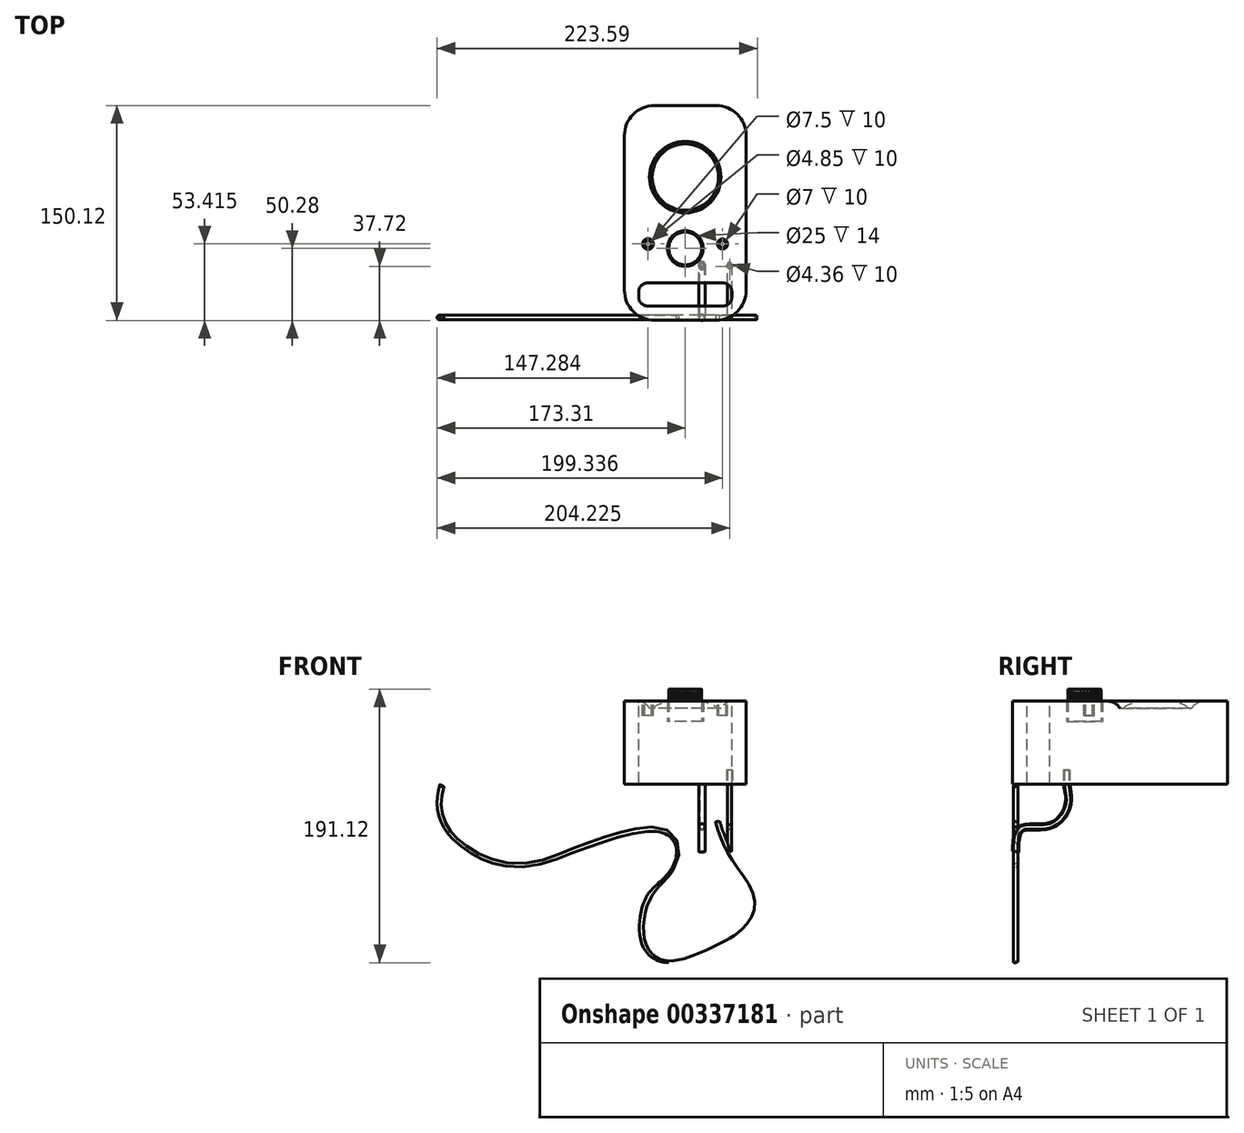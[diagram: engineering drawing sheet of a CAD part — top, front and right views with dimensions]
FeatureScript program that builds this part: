
annotation { "Feature Type Name" : "Feature", "Feature Type Description" : "" }
export const myFeature = defineFeature(function(context is Context, id is Id, definition is map)
    precondition{}
    {
        {
            var Q0;
            Q0=qCreatedBy(makeId("Top.planeOp"),FACE);
            var sketch = newSketch(context, id + "F0", { "sketchPlane" : qUnion([Q0])});
            skLineSegment(sketch, "E0.bottom", {"start": v(0, 150) * mm, "end": v(85, 150) * mm});
            skLineSegment(sketch, "E0.top", {"start": v(0, 0) * mm, "end": v(85, 0) * mm});
            skLineSegment(sketch, "E0.left", {"start": v(0, 150) * mm, "end": v(0, 0) * mm});
            skLineSegment(sketch, "E0.right", {"start": v(85, 150) * mm, "end": v(85, 0) * mm});
            skCircle(sketch, "E1", {"center": v(42.5, 100) * mm, "radius": 25 * mm});
            skLineSegment(sketch, "E2", {"start": v(42.5, 100) * mm, "end": v(-105.98, 100) * mm});
            skSolve(sketch);
        }
        {
            var Q0;
            Q0=makeQuery(id+"F0.imprint","IMPRINT",FACE,{"disambiguationData":[TD([[makeQuery(id+"F0.imprint","IMPRINT",EDGE,{"derivedFrom":sQuery(id+"F0.wireOp",EDGE,"E1")}),1.0]])]});
            extrude(context, id + "F1", {"entities" : qUnion([Q0]), "depth" : 53 * mm});
        }
        {
            var Q0;
            {var subQ1=sQuery(id+"F0.wireOp",EDGE,"E0.bottom");Q0=makeQuery(id+"F0.imprint","IMPRINT",FACE,{"disambiguationData":[TD([[makeQuery(id+"F0.imprint","IMPRINT",EDGE,{"derivedFrom":subQ1}),-1.0]])]});}
            extrude(context, id + "F2", {"entities" : qUnion([Q0]), "operationType" : NewBodyOperationType.ADD, "depth" : 58 * mm});
        }
        {
            var Q0;
            Q0=makeQuery(id+"F2.opExtrude","CAP_FACE",FACE,{"disambiguationData":[OSD([sQuery(id+"F0.wireOp",EDGE,"E0.bottom"),sQuery(id+"F0.wireOp",EDGE,"E0.top"),sQuery(id+"F0.wireOp",EDGE,"E0.left"),sQuery(id+"F0.wireOp",EDGE,"E0.right"),sQuery(id+"F0.wireOp",EDGE,"E1")])],"isStart":false});
            var sketch = newSketch(context, id + "F3", { "sketchPlane" : qUnion([Q0])});
            skLineSegment(sketch, "E3.bottom", {"start": v(42.5, 10) * mm, "end": v(16, 10) * mm});
            skLineSegment(sketch, "E3.top", {"start": v(42.5, 26) * mm, "end": v(16, 26) * mm});
            skLineSegment(sketch, "E3.right", {"start": v(10, 16) * mm, "end": v(10, 20) * mm});
            skPoint(sketch, "E4.visualSharp", {"position": v(10, 26) * mm});
            skArc(sketch, "E4.filletArc", {"start": v(16, 26) * mm, "mid": v(11.76, 24.24) * mm, "end": v(10, 20) * mm});
            skPoint(sketch, "E5.visualSharp", {"position": v(10, 10) * mm});
            skArc(sketch, "E5.filletArc", {"start": v(10, 16) * mm, "mid": v(11.76, 11.76) * mm, "end": v(16, 10) * mm});
            skArc(sketch, "E6.MirrorCS", {"start": v(69, 26) * mm, "mid": v(73.24, 24.24) * mm, "end": v(75, 20) * mm});
            skArc(sketch, "E7.MirrorCS", {"start": v(75, 16) * mm, "mid": v(73.24, 11.76) * mm, "end": v(69, 10) * mm});
            skLineSegment(sketch, "E8.MirrorCS", {"start": v(75, 16) * mm, "end": v(75, 20) * mm});
            skLineSegment(sketch, "E9.MirrorCS", {"start": v(42.5, 26) * mm, "end": v(69, 26) * mm});
            skLineSegment(sketch, "E10.MirrorCS", {"start": v(42.5, 10) * mm, "end": v(69, 10) * mm});
            skSolve(sketch);
        }
        {
            var Q0;
            Q0=makeQuery(id+"F2.opExtrude","CAP_EDGE",EDGE,{"disambiguationData":[OSD([sQuery(id+"F0.wireOp",EDGE,"E1")])],"isStart":false});
            fillet(context, id + "F4", {"entities" : qUnion([Q0]), "radius" : 10 * mm, "tangentPropagation" : true, "allowEdgeOverflow" : false});
        }
        {
            var Q0;
            Q0=makeQuery(id+"F2.opExtrude","SWEPT_EDGE",EDGE,{"disambiguationData":[OSD([sQuery(id+"F0.wireOp",EDGE,"E0.bottom"),sQuery(id+"F0.wireOp",EDGE,"E0.right")])]});
            var Q1;
            Q1=makeQuery(id+"F2.opExtrude","SWEPT_EDGE",EDGE,{"disambiguationData":[OSD([sQuery(id+"F0.wireOp",EDGE,"E0.top"),sQuery(id+"F0.wireOp",EDGE,"E0.right")])]});
            var Q2;
            Q2=makeQuery(id+"F2.opExtrude","SWEPT_EDGE",EDGE,{"disambiguationData":[OSD([sQuery(id+"F0.wireOp",EDGE,"E0.top"),sQuery(id+"F0.wireOp",EDGE,"E0.left")])]});
            var Q3;
            Q3=makeQuery(id+"F2.opExtrude","SWEPT_EDGE",EDGE,{"disambiguationData":[OSD([sQuery(id+"F0.wireOp",EDGE,"E0.bottom"),sQuery(id+"F0.wireOp",EDGE,"E0.left")])]});
            fillet(context, id + "F5", {"entities" : qUnion([Q0, Q1, Q2, Q3]), "radius" : 21 * mm, "tangentPropagation" : true, "allowEdgeOverflow" : false});
        }
        {
            var Q0;
            Q0=makeQuery(id+"F3.imprint","IMPRINT",FACE,{"disambiguationData":[TD([[makeQuery(id+"F3.imprint","IMPRINT",EDGE,{"derivedFrom":sQuery(id+"F3.wireOp",EDGE,"E3.bottom")}),-1.0]])]});
            extrude(context, id + "F6", {"entities" : qUnion([Q0]), "operationType" : NewBodyOperationType.REMOVE, "oppositeDirection" : true, "depth" : 60 * mm});
        }
        {
            var Q0;
            Q0=makeQuery(id+"F6.boolean.opBoolean","COPY",EDGE,{"derivedFrom":makeQuery(id+"F6.opExtrude","CAP_EDGE",EDGE,{"disambiguationData":[OSD([sQuery(id+"F3.wireOp",EDGE,"E3.top"),sQuery(id+"F3.wireOp",EDGE,"E9.MirrorCS")])],"isStart":true})});
            var Q1;
            Q1=makeQuery(id+"F6.boolean.opBoolean","COPY",EDGE,{"derivedFrom":makeQuery(id+"F6.opExtrude","CAP_EDGE",EDGE,{"disambiguationData":[OSD([sQuery(id+"F3.wireOp",EDGE,"E3.bottom"),sQuery(id+"F3.wireOp",EDGE,"E10.MirrorCS")])],"isStart":true})});
            var Q2;
            {var subQ0=sQuery(id+"F0.wireOp",EDGE,"E1");Q2=makeQuery(id+"F6.boolean.opBoolean","INTERSECT",EDGE,{"derivedFrom":[makeQuery(id+"F2.boolean.opBoolean","MERGE",FACE,{"derivedFrom":[makeQuery(id+"F1.opExtrude","CAP_FACE",FACE,{"disambiguationData":[OSD([subQ0])],"isStart":true}),makeQuery(id+"F2.opExtrude","CAP_FACE",FACE,{"disambiguationData":[OSD([sQuery(id+"F0.wireOp",EDGE,"E0.bottom"),sQuery(id+"F0.wireOp",EDGE,"E0.top"),sQuery(id+"F0.wireOp",EDGE,"E0.left"),sQuery(id+"F0.wireOp",EDGE,"E0.right"),subQ0])],"isStart":true})]}),makeQuery(id+"F6.opExtrude","SWEPT_FACE",FACE,{"disambiguationData":[OSD([sQuery(id+"F3.wireOp",EDGE,"E3.top"),sQuery(id+"F3.wireOp",EDGE,"E9.MirrorCS")])]})]});}
            fillet(context, id + "F7", {"entities" : qUnion([Q0, Q1, Q2]), "radius" : 1 * mm, "tangentPropagation" : true, "allowEdgeOverflow" : false});
        }
        {
            var Q0;
            Q0=makeQuery(id+"F2.opExtrude","CAP_FACE",FACE,{"disambiguationData":[OSD([sQuery(id+"F0.wireOp",EDGE,"E0.bottom"),sQuery(id+"F0.wireOp",EDGE,"E0.top"),sQuery(id+"F0.wireOp",EDGE,"E0.left"),sQuery(id+"F0.wireOp",EDGE,"E0.right"),sQuery(id+"F0.wireOp",EDGE,"E1")])],"isStart":false});
            var sketch = newSketch(context, id + "F8", { "sketchPlane" : qUnion([Q0])});
            skCircle(sketch, "E11", {"center": v(16.47, 53.3) * mm, "radius": 3.5 * mm});
            skLineSegment(sketch, "E12", {"start": v(42.5, 27) * mm, "end": v(42.5, 63.5) * mm});
            skCircle(sketch, "E13.0", {"center": v(16.47, 53.3) * mm, "radius": 3.75 * mm});
            skCircle(sketch, "E14", {"center": v(16.47, 53.3) * mm, "radius": 2.43 * mm});
            skCircle(sketch, "E15.MirrorC", {"center": v(68.53, 53.3) * mm, "radius": 3.5 * mm});
            skCircle(sketch, "E16.MirrorC", {"center": v(68.53, 53.3) * mm, "radius": 3.75 * mm});
            skCircle(sketch, "E17.MirrorC", {"center": v(68.53, 53.3) * mm, "radius": 2.43 * mm});
            skSolve(sketch);
        }
        {
            var Q0;
            Q0=makeQuery(id+"F8.imprint","IMPRINT",FACE,{"disambiguationData":[TD([[makeQuery(id+"F8.imprint","IMPRINT",EDGE,{"derivedFrom":sQuery(id+"F8.wireOp",EDGE,"E11")}),-1.0]])]});
            var Q1;
            Q1=makeQuery(id+"F8.imprint","IMPRINT",FACE,{"disambiguationData":[TD([[makeQuery(id+"F8.imprint","IMPRINT",EDGE,{"derivedFrom":sQuery(id+"F8.wireOp",EDGE,"E14")}),1.0]])]});
            var Q2;
            Q2=makeQuery(id+"F8.imprint","IMPRINT",FACE,{"disambiguationData":[TD([[makeQuery(id+"F8.imprint","IMPRINT",EDGE,{"derivedFrom":sQuery(id+"F8.wireOp",EDGE,"E15.MirrorC")}),1.0]])]});
            var Q3;
            Q3=makeQuery(id+"F8.imprint","IMPRINT",FACE,{"disambiguationData":[TD([[makeQuery(id+"F8.imprint","IMPRINT",EDGE,{"derivedFrom":sQuery(id+"F8.wireOp",EDGE,"E17.MirrorC")}),-1.0]])]});
            extrude(context, id + "F9", {"entities" : qUnion([Q0, Q1, Q2, Q3]), "operationType" : NewBodyOperationType.REMOVE, "oppositeDirection" : true, "depth" : 10 * mm});
        }
        {
            var Q0;
            {var subQ1=sQuery(id+"F0.wireOp",EDGE,"E0.bottom");Q0=makeQuery(id+"F0.imprint","IMPRINT",FACE,{"disambiguationData":[TD([[makeQuery(id+"F0.imprint","IMPRINT",EDGE,{"derivedFrom":subQ1}),-1.0]])]});}
            var sketch = newSketch(context, id + "F10", { "sketchPlane" : qUnion([Q0])});
            skCircle(sketch, "E18", {"center": v(42.5, 50.16) * mm, "radius": 12.5 * mm});
            skSolve(sketch);
        }
        {
            var Q0;
            Q0 = qSketchRegion(id + "F10", true);
            extrude(context, id + "F11", {"entities" : qUnion([Q0]), "operationType" : NewBodyOperationType.REMOVE, "depth" : 100 * mm, "hasSecondDirection" : true, "secondDirectionOppositeDirection" : true, "secondDirectionDepth" : -44 * mm});
        }
        {
            var Q0;
            Q0=makeQuery(id+"F11.boolean.opBoolean","COPY",FACE,{"derivedFrom":makeQuery(id+"F11.opExtrude","CAP_FACE",FACE,{"disambiguationData":[OSD([sQuery(id+"F10.wireOp",EDGE,"E18")])],"isStart":true})});
            var sketch = newSketch(context, id + "F12", { "sketchPlane" : qUnion([Q0])});
            skCircle(sketch, "E19", {"center": v(42.5, 50.16) * mm, "radius": 11.52 * mm});
            skSolve(sketch);
        }
        {
            var Q0;
            Q0=makeQuery(id+"F12.imprint","IMPRINT",FACE,{"disambiguationData":[TD([[makeQuery(id+"F12.imprint","IMPRINT",EDGE,{"derivedFrom":sQuery(id+"F12.wireOp",EDGE,"E19")}),1.0]])]});
            extrude(context, id + "F13", {"entities" : qUnion([Q0]), "depth" : 22.5 * mm});
        }
        {
            var Q0;
            Q0=makeQuery(id+"F13.opExtrude","CAP_EDGE",EDGE,{"disambiguationData":[OSD([sQuery(id+"F12.wireOp",EDGE,"E19")])],"isStart":false});
            fillet(context, id + "F14", {"entities" : qUnion([Q0]), "radius" : 0.5 * mm, "tangentPropagation" : true, "allowEdgeOverflow" : false});
        }
        {
            var Q0;
            Q0=makeQuery(id+"F13.opExtrude","CAP_FACE",FACE,{"disambiguationData":[OSD([sQuery(id+"F12.wireOp",EDGE,"E19")])],"isStart":false});
            var sketch = newSketch(context, id + "F15", { "sketchPlane" : qUnion([Q0])});
            skLineSegment(sketch, "E20", {"start": v(42.5, 61.18) * mm, "end": v(42.13, 61.81) * mm});
            skLineSegment(sketch, "E21.MirrorCS", {"start": v(42.5, 61.18) * mm, "end": v(42.87, 61.81) * mm});
            skLineSegment(sketch, "E22", {"start": v(42.13, 61.81) * mm, "end": v(42.87, 61.81) * mm});
            skPoint(sketch, "E23.start.orphan", {"position": v(42.5, 50.16) * mm});
            skLineSegment(sketch, "E24.1.0", {"start": v(41.44, 61.13) * mm, "end": v(41.75, 61.8) * mm});
            skLineSegment(sketch, "E24.1.1", {"start": v(41, 61.72) * mm, "end": v(41.75, 61.8) * mm});
            skLineSegment(sketch, "E24.1.2", {"start": v(41.44, 61.13) * mm, "end": v(41, 61.72) * mm});
            skLineSegment(sketch, "E24.2.0", {"start": v(40.38, 60.98) * mm, "end": v(40.63, 61.66) * mm});
            skLineSegment(sketch, "E24.2.1", {"start": v(39.9, 61.52) * mm, "end": v(40.63, 61.66) * mm});
            skLineSegment(sketch, "E24.2.2", {"start": v(40.38, 60.98) * mm, "end": v(39.9, 61.52) * mm});
            skLineSegment(sketch, "E25.1.3.0", {"start": v(39.35, 60.72) * mm, "end": v(39.53, 61.43) * mm});
            skLineSegment(sketch, "E25.3.3.0", {"start": v(38.81, 61.22) * mm, "end": v(39.53, 61.43) * mm});
            skLineSegment(sketch, "E25.6.3.0", {"start": v(39.35, 60.72) * mm, "end": v(38.81, 61.22) * mm});
            skLineSegment(sketch, "E25.1.4.0", {"start": v(38.34, 60.37) * mm, "end": v(38.45, 61.1) * mm});
            skLineSegment(sketch, "E25.3.4.0", {"start": v(37.76, 60.8) * mm, "end": v(38.45, 61.1) * mm});
            skLineSegment(sketch, "E25.6.4.0", {"start": v(38.34, 60.37) * mm, "end": v(37.76, 60.8) * mm});
            skLineSegment(sketch, "E25.1.5.0", {"start": v(37.38, 59.92) * mm, "end": v(37.42, 60.65) * mm});
            skLineSegment(sketch, "E25.3.5.0", {"start": v(36.75, 60.3) * mm, "end": v(37.42, 60.65) * mm});
            skLineSegment(sketch, "E25.6.5.0", {"start": v(37.38, 59.92) * mm, "end": v(36.75, 60.3) * mm});
            skLineSegment(sketch, "E25.1.6.0", {"start": v(36.46, 59.38) * mm, "end": v(36.43, 60.1) * mm});
            skLineSegment(sketch, "E25.3.6.0", {"start": v(35.8, 59.7) * mm, "end": v(36.43, 60.1) * mm});
            skLineSegment(sketch, "E25.6.6.0", {"start": v(36.46, 59.38) * mm, "end": v(35.8, 59.7) * mm});
            skLineSegment(sketch, "E25.1.7.0", {"start": v(35.6, 58.75) * mm, "end": v(35.5, 59.48) * mm});
            skLineSegment(sketch, "E25.3.7.0", {"start": v(34.91, 59) * mm, "end": v(35.5, 59.48) * mm});
            skLineSegment(sketch, "E25.6.7.0", {"start": v(35.6, 58.75) * mm, "end": v(34.91, 59) * mm});
            skLineSegment(sketch, "E25.1.8.0", {"start": v(34.8, 58.05) * mm, "end": v(34.63, 58.76) * mm});
            skLineSegment(sketch, "E25.3.8.0", {"start": v(34.1, 58.24) * mm, "end": v(34.63, 58.76) * mm});
            skLineSegment(sketch, "E25.6.8.0", {"start": v(34.8, 58.05) * mm, "end": v(34.1, 58.24) * mm});
            skLineSegment(sketch, "E25.1.9.0", {"start": v(34.08, 57.27) * mm, "end": v(33.84, 57.96) * mm});
            skLineSegment(sketch, "E25.3.9.0", {"start": v(33.35, 57.39) * mm, "end": v(33.84, 57.96) * mm});
            skLineSegment(sketch, "E25.6.9.0", {"start": v(34.08, 57.27) * mm, "end": v(33.35, 57.39) * mm});
            skLineSegment(sketch, "E25.1.10.0", {"start": v(33.43, 56.42) * mm, "end": v(33.12, 57.09) * mm});
            skLineSegment(sketch, "E25.3.10.0", {"start": v(32.7, 56.47) * mm, "end": v(33.12, 57.09) * mm});
            skLineSegment(sketch, "E25.6.10.0", {"start": v(33.43, 56.42) * mm, "end": v(32.7, 56.47) * mm});
            skLineSegment(sketch, "E25.1.11.0", {"start": v(32.87, 55.52) * mm, "end": v(32.5, 56.15) * mm});
            skLineSegment(sketch, "E25.3.11.0", {"start": v(32.14, 55.5) * mm, "end": v(32.5, 56.15) * mm});
            skLineSegment(sketch, "E25.6.11.0", {"start": v(32.87, 55.52) * mm, "end": v(32.14, 55.5) * mm});
            skLineSegment(sketch, "E25.1.12.0", {"start": v(32.4, 54.56) * mm, "end": v(31.97, 55.16) * mm});
            skLineSegment(sketch, "E25.3.12.0", {"start": v(31.67, 54.47) * mm, "end": v(31.97, 55.16) * mm});
            skLineSegment(sketch, "E25.6.12.0", {"start": v(32.4, 54.56) * mm, "end": v(31.67, 54.47) * mm});
            skLineSegment(sketch, "E25.1.13.0", {"start": v(32.02, 53.57) * mm, "end": v(31.54, 54.12) * mm});
            skLineSegment(sketch, "E25.3.13.0", {"start": v(31.3, 53.4) * mm, "end": v(31.54, 54.12) * mm});
            skLineSegment(sketch, "E25.6.13.0", {"start": v(32.02, 53.57) * mm, "end": v(31.3, 53.4) * mm});
            skLineSegment(sketch, "E25.1.14.0", {"start": v(31.74, 52.54) * mm, "end": v(31.2, 53.04) * mm});
            skLineSegment(sketch, "E25.3.14.0", {"start": v(31.04, 52.3) * mm, "end": v(31.2, 53.04) * mm});
            skLineSegment(sketch, "E25.6.14.0", {"start": v(31.74, 52.54) * mm, "end": v(31.04, 52.3) * mm});
            skLineSegment(sketch, "E25.1.15.0", {"start": v(31.56, 51.49) * mm, "end": v(30.98, 51.94) * mm});
            skLineSegment(sketch, "E25.3.15.0", {"start": v(30.89, 51.2) * mm, "end": v(30.98, 51.94) * mm});
            skLineSegment(sketch, "E25.6.15.0", {"start": v(31.56, 51.49) * mm, "end": v(30.89, 51.2) * mm});
            skLineSegment(sketch, "E25.1.16.0", {"start": v(31.48, 50.43) * mm, "end": v(30.86, 50.81) * mm});
            skLineSegment(sketch, "E25.3.16.0", {"start": v(30.84, 50.07) * mm, "end": v(30.86, 50.81) * mm});
            skLineSegment(sketch, "E25.6.16.0", {"start": v(31.48, 50.43) * mm, "end": v(30.84, 50.07) * mm});
            skLineSegment(sketch, "E25.1.17.0", {"start": v(31.5, 49.36) * mm, "end": v(30.85, 49.69) * mm});
            skLineSegment(sketch, "E25.3.17.0", {"start": v(30.9, 48.94) * mm, "end": v(30.85, 49.69) * mm});
            skLineSegment(sketch, "E25.6.17.0", {"start": v(31.5, 49.36) * mm, "end": v(30.9, 48.94) * mm});
            skLineSegment(sketch, "E25.1.18.0", {"start": v(31.64, 48.3) * mm, "end": v(30.95, 48.57) * mm});
            skLineSegment(sketch, "E25.3.18.0", {"start": v(31.08, 47.83) * mm, "end": v(30.95, 48.57) * mm});
            skLineSegment(sketch, "E25.6.18.0", {"start": v(31.64, 48.3) * mm, "end": v(31.08, 47.83) * mm});
            skLineSegment(sketch, "E25.1.19.0", {"start": v(31.87, 47.26) * mm, "end": v(31.16, 47.46) * mm});
            skLineSegment(sketch, "E25.3.19.0", {"start": v(31.36, 46.74) * mm, "end": v(31.16, 47.46) * mm});
            skLineSegment(sketch, "E25.6.19.0", {"start": v(31.87, 47.26) * mm, "end": v(31.36, 46.74) * mm});
            skLineSegment(sketch, "E25.1.20.0", {"start": v(32.2, 46.25) * mm, "end": v(31.47, 46.38) * mm});
            skLineSegment(sketch, "E25.3.20.0", {"start": v(31.74, 45.68) * mm, "end": v(31.47, 46.38) * mm});
            skLineSegment(sketch, "E25.6.20.0", {"start": v(32.2, 46.25) * mm, "end": v(31.74, 45.68) * mm});
            skLineSegment(sketch, "E25.1.21.0", {"start": v(32.62, 45.28) * mm, "end": v(31.9, 45.33) * mm});
            skLineSegment(sketch, "E25.3.21.0", {"start": v(32.22, 44.66) * mm, "end": v(31.9, 45.33) * mm});
            skLineSegment(sketch, "E25.6.21.0", {"start": v(32.62, 45.28) * mm, "end": v(32.22, 44.66) * mm});
            skLineSegment(sketch, "E25.1.22.0", {"start": v(33.14, 44.34) * mm, "end": v(32.4, 44.33) * mm});
            skLineSegment(sketch, "E25.3.22.0", {"start": v(32.8, 43.7) * mm, "end": v(32.4, 44.33) * mm});
            skLineSegment(sketch, "E25.6.22.0", {"start": v(33.14, 44.34) * mm, "end": v(32.8, 43.7) * mm});
            skLineSegment(sketch, "E25.1.23.0", {"start": v(33.74, 43.47) * mm, "end": v(33.02, 43.38) * mm});
            skLineSegment(sketch, "E25.3.23.0", {"start": v(33.47, 42.79) * mm, "end": v(33.02, 43.38) * mm});
            skLineSegment(sketch, "E25.6.23.0", {"start": v(33.74, 43.47) * mm, "end": v(33.47, 42.79) * mm});
            skLineSegment(sketch, "E25.1.24.0", {"start": v(34.43, 42.65) * mm, "end": v(33.71, 42.5) * mm});
            skLineSegment(sketch, "E25.3.24.0", {"start": v(34.22, 41.95) * mm, "end": v(33.71, 42.5) * mm});
            skLineSegment(sketch, "E25.6.24.0", {"start": v(34.43, 42.65) * mm, "end": v(34.22, 41.95) * mm});
            skLineSegment(sketch, "E25.1.25.0", {"start": v(35.2, 41.91) * mm, "end": v(34.5, 41.69) * mm});
            skLineSegment(sketch, "E25.3.25.0", {"start": v(35.05, 41.2) * mm, "end": v(34.5, 41.69) * mm});
            skLineSegment(sketch, "E25.6.25.0", {"start": v(35.2, 41.91) * mm, "end": v(35.05, 41.2) * mm});
            skLineSegment(sketch, "E25.1.26.0", {"start": v(36.02, 41.24) * mm, "end": v(35.35, 40.95) * mm});
            skLineSegment(sketch, "E25.3.26.0", {"start": v(35.95, 40.51) * mm, "end": v(35.35, 40.95) * mm});
            skLineSegment(sketch, "E25.6.26.0", {"start": v(36.02, 41.24) * mm, "end": v(35.95, 40.51) * mm});
            skLineSegment(sketch, "E25.1.27.0", {"start": v(36.91, 40.66) * mm, "end": v(36.27, 40.3) * mm});
            skLineSegment(sketch, "E25.3.27.0", {"start": v(36.92, 39.93) * mm, "end": v(36.27, 40.3) * mm});
            skLineSegment(sketch, "E25.6.27.0", {"start": v(36.91, 40.66) * mm, "end": v(36.92, 39.93) * mm});
            skLineSegment(sketch, "E25.1.28.0", {"start": v(37.86, 40.16) * mm, "end": v(37.25, 39.75) * mm});
            skLineSegment(sketch, "E25.3.28.0", {"start": v(37.93, 39.44) * mm, "end": v(37.25, 39.75) * mm});
            skLineSegment(sketch, "E25.6.28.0", {"start": v(37.86, 40.16) * mm, "end": v(37.93, 39.44) * mm});
            skLineSegment(sketch, "E25.1.29.0", {"start": v(38.84, 39.76) * mm, "end": v(38.28, 39.3) * mm});
            skLineSegment(sketch, "E25.3.29.0", {"start": v(38.99, 39.05) * mm, "end": v(38.28, 39.3) * mm});
            skLineSegment(sketch, "E25.6.29.0", {"start": v(38.84, 39.76) * mm, "end": v(38.99, 39.05) * mm});
            skLineSegment(sketch, "E25.1.30.0", {"start": v(39.86, 39.46) * mm, "end": v(39.35, 38.94) * mm});
            skLineSegment(sketch, "E25.3.30.0", {"start": v(40.07, 38.76) * mm, "end": v(39.35, 38.94) * mm});
            skLineSegment(sketch, "E25.6.30.0", {"start": v(39.86, 39.46) * mm, "end": v(40.07, 38.76) * mm});
            skLineSegment(sketch, "E25.1.31.0", {"start": v(40.9, 39.25) * mm, "end": v(40.45, 38.69) * mm});
            skLineSegment(sketch, "E25.3.31.0", {"start": v(41.19, 38.58) * mm, "end": v(40.45, 38.69) * mm});
            skLineSegment(sketch, "E25.6.31.0", {"start": v(40.9, 39.25) * mm, "end": v(41.19, 38.58) * mm});
            skLineSegment(sketch, "E25.1.32.0", {"start": v(41.97, 39.15) * mm, "end": v(41.56, 38.54) * mm});
            skLineSegment(sketch, "E25.3.32.0", {"start": v(42.31, 38.5) * mm, "end": v(41.56, 38.54) * mm});
            skLineSegment(sketch, "E25.6.32.0", {"start": v(41.97, 39.15) * mm, "end": v(42.31, 38.5) * mm});
            skLineSegment(sketch, "E25.1.33.0", {"start": v(43.03, 39.15) * mm, "end": v(42.69, 38.5) * mm});
            skLineSegment(sketch, "E25.3.33.0", {"start": v(43.44, 38.54) * mm, "end": v(42.69, 38.5) * mm});
            skLineSegment(sketch, "E25.6.33.0", {"start": v(43.03, 39.15) * mm, "end": v(43.44, 38.54) * mm});
            skLineSegment(sketch, "E25.1.34.0", {"start": v(44.1, 39.25) * mm, "end": v(43.81, 38.58) * mm});
            skLineSegment(sketch, "E25.3.34.0", {"start": v(44.55, 38.69) * mm, "end": v(43.81, 38.58) * mm});
            skLineSegment(sketch, "E25.6.34.0", {"start": v(44.1, 39.25) * mm, "end": v(44.55, 38.69) * mm});
            skLineSegment(sketch, "E25.1.35.0", {"start": v(45.14, 39.46) * mm, "end": v(44.93, 38.76) * mm});
            skLineSegment(sketch, "E25.3.35.0", {"start": v(45.65, 38.94) * mm, "end": v(44.93, 38.76) * mm});
            skLineSegment(sketch, "E25.6.35.0", {"start": v(45.14, 39.46) * mm, "end": v(45.65, 38.94) * mm});
            skLineSegment(sketch, "E25.1.36.0", {"start": v(46.16, 39.76) * mm, "end": v(46.01, 39.05) * mm});
            skLineSegment(sketch, "E25.3.36.0", {"start": v(46.72, 39.3) * mm, "end": v(46.01, 39.05) * mm});
            skLineSegment(sketch, "E25.6.36.0", {"start": v(46.16, 39.76) * mm, "end": v(46.72, 39.3) * mm});
            skLineSegment(sketch, "E25.1.37.0", {"start": v(47.14, 40.16) * mm, "end": v(47.07, 39.44) * mm});
            skLineSegment(sketch, "E25.3.37.0", {"start": v(47.75, 39.75) * mm, "end": v(47.07, 39.44) * mm});
            skLineSegment(sketch, "E25.6.37.0", {"start": v(47.14, 40.16) * mm, "end": v(47.75, 39.75) * mm});
            skLineSegment(sketch, "E25.1.38.0", {"start": v(48.09, 40.66) * mm, "end": v(48.08, 39.93) * mm});
            skLineSegment(sketch, "E25.3.38.0", {"start": v(48.73, 40.3) * mm, "end": v(48.08, 39.93) * mm});
            skLineSegment(sketch, "E25.6.38.0", {"start": v(48.09, 40.66) * mm, "end": v(48.73, 40.3) * mm});
            skLineSegment(sketch, "E25.1.39.0", {"start": v(48.98, 41.24) * mm, "end": v(49.05, 40.51) * mm});
            skLineSegment(sketch, "E25.3.39.0", {"start": v(49.65, 40.95) * mm, "end": v(49.05, 40.51) * mm});
            skLineSegment(sketch, "E25.6.39.0", {"start": v(48.98, 41.24) * mm, "end": v(49.65, 40.95) * mm});
            skLineSegment(sketch, "E25.1.40.0", {"start": v(49.8, 41.91) * mm, "end": v(49.95, 41.2) * mm});
            skLineSegment(sketch, "E25.3.40.0", {"start": v(50.5, 41.69) * mm, "end": v(49.95, 41.2) * mm});
            skLineSegment(sketch, "E25.6.40.0", {"start": v(49.8, 41.91) * mm, "end": v(50.5, 41.69) * mm});
            skLineSegment(sketch, "E25.1.41.0", {"start": v(50.57, 42.65) * mm, "end": v(50.78, 41.95) * mm});
            skLineSegment(sketch, "E25.3.41.0", {"start": v(51.29, 42.5) * mm, "end": v(50.78, 41.95) * mm});
            skLineSegment(sketch, "E25.6.41.0", {"start": v(50.57, 42.65) * mm, "end": v(51.29, 42.5) * mm});
            skLineSegment(sketch, "E25.1.42.0", {"start": v(51.26, 43.47) * mm, "end": v(51.53, 42.79) * mm});
            skLineSegment(sketch, "E25.3.42.0", {"start": v(51.98, 43.38) * mm, "end": v(51.53, 42.79) * mm});
            skLineSegment(sketch, "E25.6.42.0", {"start": v(51.26, 43.47) * mm, "end": v(51.98, 43.38) * mm});
            skLineSegment(sketch, "E25.1.43.0", {"start": v(51.86, 44.34) * mm, "end": v(52.2, 43.7) * mm});
            skLineSegment(sketch, "E25.3.43.0", {"start": v(52.6, 44.33) * mm, "end": v(52.2, 43.7) * mm});
            skLineSegment(sketch, "E25.6.43.0", {"start": v(51.86, 44.34) * mm, "end": v(52.6, 44.33) * mm});
            skLineSegment(sketch, "E25.1.44.0", {"start": v(52.38, 45.28) * mm, "end": v(52.78, 44.66) * mm});
            skLineSegment(sketch, "E25.3.44.0", {"start": v(53.1, 45.33) * mm, "end": v(52.78, 44.66) * mm});
            skLineSegment(sketch, "E25.6.44.0", {"start": v(52.38, 45.28) * mm, "end": v(53.1, 45.33) * mm});
            skLineSegment(sketch, "E25.1.45.0", {"start": v(52.8, 46.25) * mm, "end": v(53.26, 45.68) * mm});
            skLineSegment(sketch, "E25.3.45.0", {"start": v(53.53, 46.38) * mm, "end": v(53.26, 45.68) * mm});
            skLineSegment(sketch, "E25.6.45.0", {"start": v(52.8, 46.25) * mm, "end": v(53.53, 46.38) * mm});
            skLineSegment(sketch, "E25.1.46.0", {"start": v(53.13, 47.26) * mm, "end": v(53.64, 46.74) * mm});
            skLineSegment(sketch, "E25.3.46.0", {"start": v(53.84, 47.46) * mm, "end": v(53.64, 46.74) * mm});
            skLineSegment(sketch, "E25.6.46.0", {"start": v(53.13, 47.26) * mm, "end": v(53.84, 47.46) * mm});
            skLineSegment(sketch, "E25.1.47.0", {"start": v(53.36, 48.3) * mm, "end": v(53.92, 47.83) * mm});
            skLineSegment(sketch, "E25.3.47.0", {"start": v(54.05, 48.57) * mm, "end": v(53.92, 47.83) * mm});
            skLineSegment(sketch, "E25.6.47.0", {"start": v(53.36, 48.3) * mm, "end": v(54.05, 48.57) * mm});
            skLineSegment(sketch, "E25.1.48.0", {"start": v(53.5, 49.36) * mm, "end": v(54.1, 48.94) * mm});
            skLineSegment(sketch, "E25.3.48.0", {"start": v(54.15, 49.69) * mm, "end": v(54.1, 48.94) * mm});
            skLineSegment(sketch, "E25.6.48.0", {"start": v(53.5, 49.36) * mm, "end": v(54.15, 49.69) * mm});
            skLineSegment(sketch, "E25.1.49.0", {"start": v(53.52, 50.43) * mm, "end": v(54.16, 50.07) * mm});
            skLineSegment(sketch, "E25.3.49.0", {"start": v(54.14, 50.81) * mm, "end": v(54.16, 50.07) * mm});
            skLineSegment(sketch, "E25.6.49.0", {"start": v(53.52, 50.43) * mm, "end": v(54.14, 50.81) * mm});
            skLineSegment(sketch, "E26.1.50.0", {"start": v(53.44, 51.49) * mm, "end": v(54.11, 51.2) * mm});
            skLineSegment(sketch, "E26.3.50.0", {"start": v(54.02, 51.94) * mm, "end": v(54.11, 51.2) * mm});
            skLineSegment(sketch, "E26.6.50.0", {"start": v(53.44, 51.49) * mm, "end": v(54.02, 51.94) * mm});
            skLineSegment(sketch, "E26.1.51.0", {"start": v(53.26, 52.54) * mm, "end": v(53.96, 52.3) * mm});
            skLineSegment(sketch, "E26.3.51.0", {"start": v(53.8, 53.04) * mm, "end": v(53.96, 52.3) * mm});
            skLineSegment(sketch, "E26.6.51.0", {"start": v(53.26, 52.54) * mm, "end": v(53.8, 53.04) * mm});
            skLineSegment(sketch, "E26.1.52.0", {"start": v(52.98, 53.57) * mm, "end": v(53.7, 53.4) * mm});
            skLineSegment(sketch, "E26.3.52.0", {"start": v(53.46, 54.12) * mm, "end": v(53.7, 53.4) * mm});
            skLineSegment(sketch, "E26.6.52.0", {"start": v(52.98, 53.57) * mm, "end": v(53.46, 54.12) * mm});
            skLineSegment(sketch, "E26.1.53.0", {"start": v(52.6, 54.56) * mm, "end": v(53.33, 54.47) * mm});
            skLineSegment(sketch, "E26.3.53.0", {"start": v(53.03, 55.16) * mm, "end": v(53.33, 54.47) * mm});
            skLineSegment(sketch, "E26.6.53.0", {"start": v(52.6, 54.56) * mm, "end": v(53.03, 55.16) * mm});
            skLineSegment(sketch, "E26.1.54.0", {"start": v(52.13, 55.52) * mm, "end": v(52.86, 55.5) * mm});
            skLineSegment(sketch, "E26.3.54.0", {"start": v(52.5, 56.15) * mm, "end": v(52.86, 55.5) * mm});
            skLineSegment(sketch, "E26.6.54.0", {"start": v(52.13, 55.52) * mm, "end": v(52.5, 56.15) * mm});
            skLineSegment(sketch, "E26.1.55.0", {"start": v(51.57, 56.42) * mm, "end": v(52.3, 56.47) * mm});
            skLineSegment(sketch, "E26.3.55.0", {"start": v(51.88, 57.09) * mm, "end": v(52.3, 56.47) * mm});
            skLineSegment(sketch, "E26.6.55.0", {"start": v(51.57, 56.42) * mm, "end": v(51.88, 57.09) * mm});
            skLineSegment(sketch, "E26.1.56.0", {"start": v(50.92, 57.27) * mm, "end": v(51.65, 57.39) * mm});
            skLineSegment(sketch, "E26.3.56.0", {"start": v(51.16, 57.96) * mm, "end": v(51.65, 57.39) * mm});
            skLineSegment(sketch, "E26.6.56.0", {"start": v(50.92, 57.27) * mm, "end": v(51.16, 57.96) * mm});
            skLineSegment(sketch, "E26.1.57.0", {"start": v(50.2, 58.05) * mm, "end": v(50.9, 58.24) * mm});
            skLineSegment(sketch, "E26.3.57.0", {"start": v(50.37, 58.76) * mm, "end": v(50.9, 58.24) * mm});
            skLineSegment(sketch, "E26.6.57.0", {"start": v(50.2, 58.05) * mm, "end": v(50.37, 58.76) * mm});
            skLineSegment(sketch, "E26.1.58.0", {"start": v(49.4, 58.75) * mm, "end": v(50.09, 59) * mm});
            skLineSegment(sketch, "E26.3.58.0", {"start": v(49.5, 59.48) * mm, "end": v(50.09, 59) * mm});
            skLineSegment(sketch, "E26.6.58.0", {"start": v(49.4, 58.75) * mm, "end": v(49.5, 59.48) * mm});
            skLineSegment(sketch, "E26.1.59.0", {"start": v(48.54, 59.38) * mm, "end": v(49.2, 59.7) * mm});
            skLineSegment(sketch, "E26.3.59.0", {"start": v(48.57, 60.1) * mm, "end": v(49.2, 59.7) * mm});
            skLineSegment(sketch, "E26.6.59.0", {"start": v(48.54, 59.38) * mm, "end": v(48.57, 60.1) * mm});
            skLineSegment(sketch, "E27.1.60.0", {"start": v(47.62, 59.92) * mm, "end": v(48.25, 60.3) * mm});
            skLineSegment(sketch, "E27.3.60.0", {"start": v(47.58, 60.65) * mm, "end": v(48.25, 60.3) * mm});
            skLineSegment(sketch, "E27.6.60.0", {"start": v(47.62, 59.92) * mm, "end": v(47.58, 60.65) * mm});
            skLineSegment(sketch, "E27.1.61.0", {"start": v(46.66, 60.37) * mm, "end": v(47.24, 60.8) * mm});
            skLineSegment(sketch, "E27.3.61.0", {"start": v(46.55, 61.1) * mm, "end": v(47.24, 60.8) * mm});
            skLineSegment(sketch, "E27.6.61.0", {"start": v(46.66, 60.37) * mm, "end": v(46.55, 61.1) * mm});
            skLineSegment(sketch, "E27.1.62.0", {"start": v(45.65, 60.72) * mm, "end": v(46.19, 61.22) * mm});
            skLineSegment(sketch, "E27.3.62.0", {"start": v(45.47, 61.43) * mm, "end": v(46.19, 61.22) * mm});
            skLineSegment(sketch, "E27.6.62.0", {"start": v(45.65, 60.72) * mm, "end": v(45.47, 61.43) * mm});
            skLineSegment(sketch, "E27.1.63.0", {"start": v(44.62, 60.98) * mm, "end": v(45.1, 61.52) * mm});
            skLineSegment(sketch, "E27.3.63.0", {"start": v(44.37, 61.66) * mm, "end": v(45.1, 61.52) * mm});
            skLineSegment(sketch, "E27.6.63.0", {"start": v(44.62, 60.98) * mm, "end": v(44.37, 61.66) * mm});
            skLineSegment(sketch, "E27.1.64.0", {"start": v(43.56, 61.13) * mm, "end": v(44, 61.72) * mm});
            skLineSegment(sketch, "E27.3.64.0", {"start": v(43.25, 61.8) * mm, "end": v(44, 61.72) * mm});
            skLineSegment(sketch, "E27.6.64.0", {"start": v(43.56, 61.13) * mm, "end": v(43.25, 61.8) * mm});
            skSolve(sketch);
        }
        {
            var Q0;
            Q0 = qSketchRegion(id + "F15", true);
            extrude(context, id + "F16", {"entities" : qUnion([Q0]), "operationType" : NewBodyOperationType.REMOVE, "oppositeDirection" : true, "depth" : 7 * mm, "hasSecondDirection" : true, "secondDirectionOppositeDirection" : false, "secondDirectionDepth" : -2 * mm});
        }
        {
            var Q0;
            {var subQ1=sQuery(id+"F0.wireOp",EDGE,"E0.bottom");Q0=makeQuery(id+"F0.imprint","IMPRINT",FACE,{"disambiguationData":[TD([[makeQuery(id+"F0.imprint","IMPRINT",EDGE,{"derivedFrom":subQ1}),-1.0]])]});}
            var sketch = newSketch(context, id + "F17", { "sketchPlane" : qUnion([Q0])});
            skCircle(sketch, "E28", {"center": v(73.42, 37.6) * mm, "radius": 2.18 * mm});
            skCircle(sketch, "E29", {"center": v(73.42, 37.6) * mm, "radius": 1.55 * mm});
            skCircle(sketch, "E30.MirrorC", {"center": v(54.13, 37.6) * mm, "radius": 1.55 * mm});
            skCircle(sketch, "E31.MirrorC", {"center": v(54.13, 37.6) * mm, "radius": 2.18 * mm});
            skSolve(sketch);
        }
        {
            var Q0;
            Q0=makeQuery(id+"F17.imprint","IMPRINT",FACE,{"disambiguationData":[TD([[makeQuery(id+"F17.imprint","IMPRINT",EDGE,{"derivedFrom":sQuery(id+"F17.wireOp",EDGE,"E28")}),1.0]])]});
            extrude(context, id + "F18", {"entities" : qUnion([Q0]), "operationType" : NewBodyOperationType.REMOVE, "depth" : 10 * mm});
        }
        {
            var Q0;
            Q0=makeQuery(id+"F2.opExtrude","SWEPT_FACE",FACE,{"disambiguationData":[OSD([sQuery(id+"F0.wireOp",EDGE,"E0.left")])]});
            var sketch = newSketch(context, id + "F19", { "sketchPlane" : qUnion([Q0])});
            skFitSpline(sketch, "E32", {"points": [v(-37.5, -2.18) * mm, v(-37.74, -15.14) * mm, v(-25.87, -28.34) * mm, v(-5.89, -30.88) * mm, v(-1.53, -49.17) * mm], "startDerivative": vector(-10.32, -58.07) * mm, "endDerivative": vector(0.54, -89.18) * mm});
            skSolve(sketch);
        }
        {
            var Q0;
            Q0=makeQuery(id+"F17.imprint","IMPRINT",FACE,{"disambiguationData":[TD([[makeQuery(id+"F17.imprint","IMPRINT",EDGE,{"derivedFrom":sQuery(id+"F17.wireOp",EDGE,"E29")}),1.0]])]});
            var Q1;
            Q1=makeQuery(id+"F17.imprint","IMPRINT",FACE,{"disambiguationData":[TD([[makeQuery(id+"F17.imprint","IMPRINT",EDGE,{"derivedFrom":sQuery(id+"F17.wireOp",EDGE,"E30.MirrorC")}),-1.0]])]});
            var Q2;
            Q2=sQuery(id+"F19.wireOp",EDGE,"E32");
            sweep(context, id + "F20", {"profiles" : qUnion([Q0, Q1]), "path" : qUnion([Q2])});
        }
        {
            var Q0;
            Q0=makeQuery(id+"F2.opExtrude","SWEPT_FACE",FACE,{"disambiguationData":[OSD([sQuery(id+"F0.wireOp",EDGE,"E0.bottom")])]});
            var sketch = newSketch(context, id + "F21", { "sketchPlane" : qUnion([Q0])});
            skFitSpline(sketch, "E33", {"points": [v(-72.98, -52.8) * mm, v(-71.53, -102.16) * mm, v(-17.27, -100.7) * mm, v(-14.91, -39.2) * mm, v(74.54, -50.26) * mm, v(123.72, -14.52) * mm, v(120.45, 25.58) * mm], "startDerivative": vector(-105.48, -377.05) * mm, "endDerivative": vector(-81.34, 285.27) * mm});
            skSolve(sketch);
        }
        {
            var Q0;
            Q0=makeQuery(id+"F20.opSweep","CAP_FACE",FACE,{"disambiguationData":[OSD([sQuery(id+"F17.wireOp",EDGE,"E29"),sQuery(id+"F19.wireOp",VERTEX,"E32.end")])],"isStart":false});
            var Q1;
            Q1=sQuery(id+"F21.wireOp",EDGE,"E33");
            sweep(context, id + "F22", {"operationType" : NewBodyOperationType.ADD, "profiles" : qUnion([Q0]), "path" : qUnion([Q1])});
        }
        {
            var Q0;
            Q0=makeQuery(id+"F1.opExtrude","CAP_FACE",FACE,{"disambiguationData":[OSD([sQuery(id+"F0.wireOp",EDGE,"E1")])],"isStart":false});
            var sketch = newSketch(context, id + "F23", { "sketchPlane" : qUnion([Q0])});
            skCircle(sketch, "E34", {"center": v(42.5, 100) * mm, "radius": 23.14 * mm});
            skSolve(sketch);
        }
        {
            var Q0;
            Q0=makeQuery(id+"F23.imprint","IMPRINT",FACE,{"disambiguationData":[TD([[makeQuery(id+"F23.imprint","IMPRINT",EDGE,{"derivedFrom":sQuery(id+"F23.wireOp",EDGE,"E34")}),1.0]])]});
            extrude(context, id + "F24", {"entities" : qUnion([Q0]), "depth" : 5 * mm});
        }
        {
            var Q0;
            Q0=makeQuery(id+"F24.opExtrude","CAP_FACE",FACE,{"disambiguationData":[OSD([sQuery(id+"F23.wireOp",EDGE,"E34")])],"isStart":false});
            fillet(context, id + "F25", {"entities" : qUnion([Q0]), "radius" : 23 * mm, "tangentPropagation" : true, "allowEdgeOverflow" : false});
        }
    });
